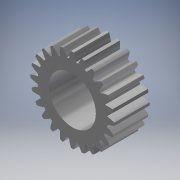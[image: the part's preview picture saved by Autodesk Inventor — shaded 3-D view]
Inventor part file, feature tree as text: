
AUTODESK INVENTOR PART (.ipt)
format: ipt  version: 2019 (Build 230136000, 136)  size: 249,344 bytes
history: native  units: mm (DEFAULTED — no unit token found)
features: plane x3, other x3, sketch x3, extrude x2
ambient origin geometry x8: Origin, YZ Plane, XZ Plane, XY Plane, X Axis, Y Axis, Z Axis, Center Point
bodies: Solid1 (feature_tree)
feature tree (11):
  extrude  "Extrusion1"  Depth=15.0mm TaperAngle=0.0deg
  plane  "Work Plane2"
  plane  "Work Plane8"
  plane  "Work Plane9"
  other  "正齒輪"
  extrude  "擠出2"  Depth=10.0mm TaperAngle=0.0deg
  sketch  "Sketch1"  dims[d0=35.714032mm d1=15.0mm d2=0.0mm]
  sketch  "Sketch2"  dims[d3=33.355289mm d4=10.0mm d5=0.0mm d16=43.083915mm d17=0.0mm d34=1.308997mm d39=0.0mm d41=0.0mm d43=43.083915mm d46=43.083915mm d47=0.0mm d48=0.0mm d49=20.0mm d50=29.0mm d51=0.0mm d59=1.0mm d60=1.0mm d61=1.0mm d62=0.15mm d63=0.25mm d64=0.375mm d65=14.3117mm d66=0.75mm d67=20.594885mm d68=0.0625mm d69=0.75mm d70=0.375mm]
  other  "Srf1"
  sketch  "草圖3"
  other  "節圓直徑"
